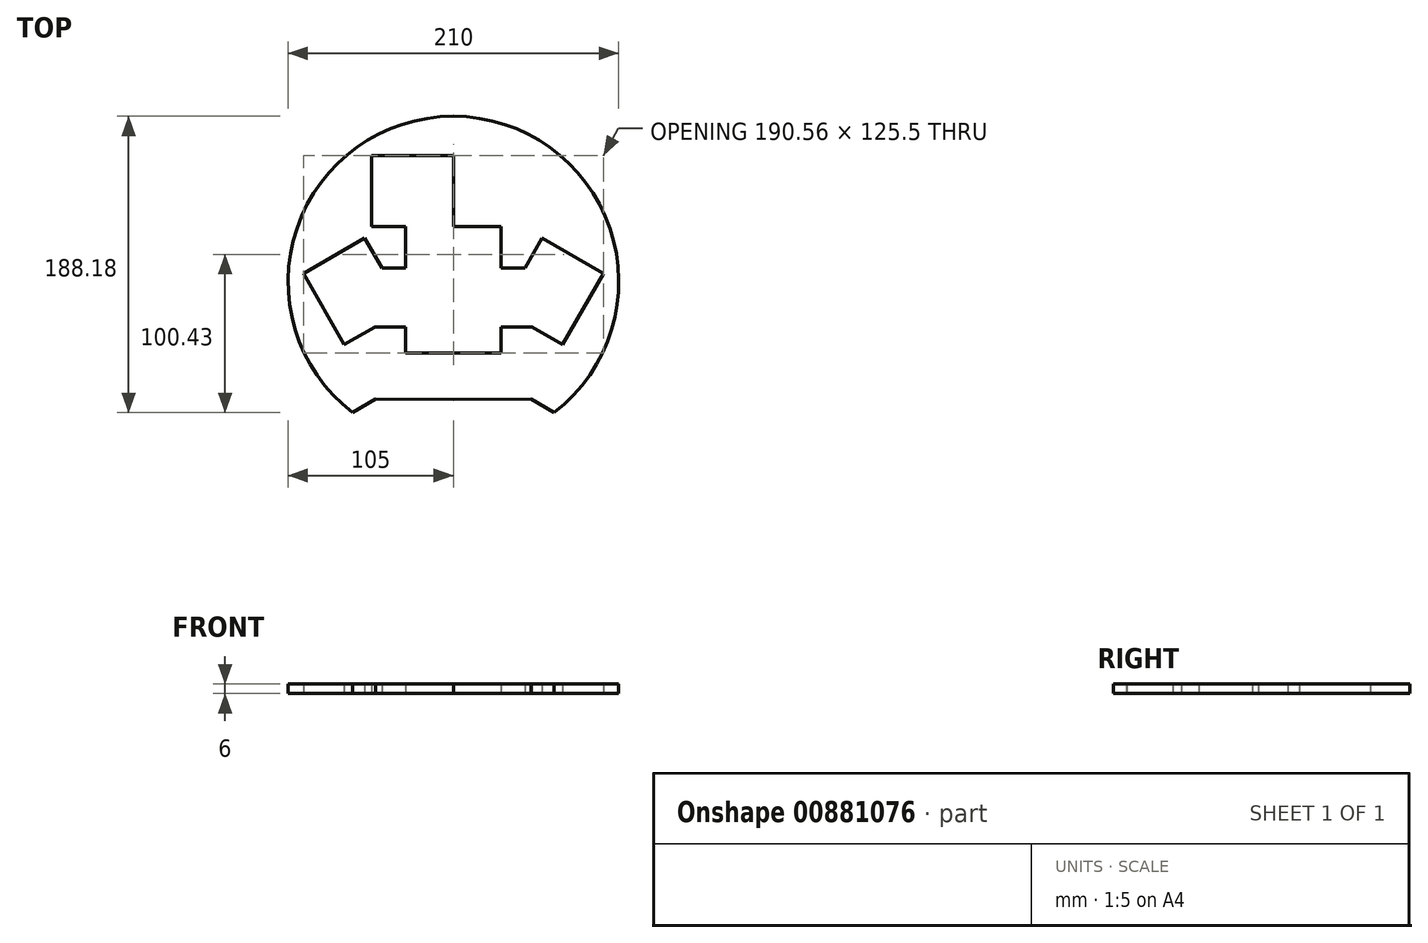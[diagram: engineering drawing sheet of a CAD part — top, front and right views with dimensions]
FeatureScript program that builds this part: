
annotation { "Feature Type Name" : "Feature", "Feature Type Description" : "" }
export const myFeature = defineFeature(function(context is Context, id is Id, definition is map)
    precondition{}
    {
        {
            var Q0;
            Q0=qCreatedBy(makeId("Top.planeOp"),FACE);
            var sketch = newSketch(context, id + "F0", { "sketchPlane" : qUnion([Q0])});
            skCircle(sketch, "E0", {"center": v(0, 0) * mm, "radius": 105 * mm});
            skLineSegment(sketch, "E1", {"start": v(-69.28, -40) * mm, "end": v(-89.28, -5.36) * mm});
            skLineSegment(sketch, "E2", {"start": v(-49.28, -74.64) * mm, "end": v(-64.08, -83.18) * mm});
            skLineSegment(sketch, "E3", {"start": v(69.28, -40) * mm, "end": v(89.28, -5.36) * mm});
            skLineSegment(sketch, "E4", {"start": v(49.28, -74.64) * mm, "end": v(64.08, -83.18) * mm});
            skLineSegment(sketch, "E5", {"start": v(0, -75) * mm, "end": v(49.28, -74.64) * mm});
            skLineSegment(sketch, "E6", {"start": v(-49.28, -74.64) * mm, "end": v(0, -75) * mm});
            skLineSegment(sketch, "E7", {"start": v(0, 80) * mm, "end": v(0, 35) * mm});
            skLineSegment(sketch, "E8", {"start": v(-69.28, -40) * mm, "end": v(-30.31, -17.5) * mm});
            skLineSegment(sketch, "E9", {"start": v(69.28, -40) * mm, "end": v(30.31, -17.5) * mm});
            skLineSegment(sketch, "E10", {"start": v(-30.31, 35) * mm, "end": v(-30.31, -17.5) * mm});
            skLineSegment(sketch, "E11", {"start": v(30.31, -17.5) * mm, "end": v(30.31, 35) * mm});
            skLineSegment(sketch, "E12", {"start": v(-30.31, -17.5) * mm, "end": v(-56.31, 27.53) * mm});
            skLineSegment(sketch, "E13", {"start": v(-56.31, 27.53) * mm, "end": v(-95.28, 5.03) * mm});
            skLineSegment(sketch, "E14", {"start": v(-95.28, 5.03) * mm, "end": v(-89.28, -5.36) * mm});
            skLineSegment(sketch, "E15", {"start": v(30.31, -17.5) * mm, "end": v(56.31, 27.53) * mm});
            skLineSegment(sketch, "E16", {"start": v(56.31, 27.53) * mm, "end": v(95.28, 5.03) * mm});
            skLineSegment(sketch, "E17", {"start": v(95.28, 5.03) * mm, "end": v(89.28, -5.36) * mm});
            skLineSegment(sketch, "E18", {"start": v(-52, 35) * mm, "end": v(-52, 80) * mm});
            skLineSegment(sketch, "E19", {"start": v(-52, 80) * mm, "end": v(0, 80) * mm});
            skLineSegment(sketch, "E20", {"start": v(-30.31, -17.5) * mm, "end": v(-30.31, -45.5) * mm});
            skLineSegment(sketch, "E21", {"start": v(-30.31, -45.5) * mm, "end": v(30.31, -45.5) * mm});
            skLineSegment(sketch, "E22", {"start": v(30.31, -45.5) * mm, "end": v(30.31, -17.5) * mm});
            skLineSegment(sketch, "E23", {"start": v(-52, 35) * mm, "end": v(-30.31, 35) * mm});
            skLineSegment(sketch, "E24", {"start": v(0, 35) * mm, "end": v(30.31, 35) * mm});
            skLineSegment(sketch, "E25", {"start": v(-30.31, 8.75) * mm, "end": v(-45.47, 8.75) * mm});
            skLineSegment(sketch, "E26", {"start": v(-45.47, 8.75) * mm, "end": v(45.47, 8.75) * mm});
            skLineSegment(sketch, "E27", {"start": v(-49.8, -28.75) * mm, "end": v(49.8, -28.75) * mm});
            skSolve(sketch);
        }
        {
            var Q0;
            {var subQ15=sQuery(id+"F0.wireOp",EDGE,"E1");Q0=makeQuery(id+"F0.imprint","IMPRINT",FACE,{"disambiguationData":[TD([[makeQuery(id+"F0.imprint","IMPRINT",EDGE,{"derivedFrom":subQ15}),1.0]])]});}
            extrude(context, id + "F1", {"entities" : qUnion([Q0]), "depth" : 6 * mm, "offsetDistance" : 25 * mm});
        }
    });
